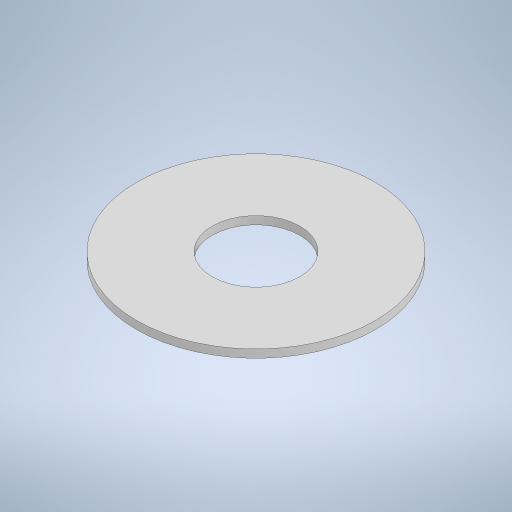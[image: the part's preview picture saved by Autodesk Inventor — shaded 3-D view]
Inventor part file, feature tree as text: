
AUTODESK INVENTOR PART (.ipt)
format: ipt  version: 2024.2 (Build 282272000, 272)  size: 224,256 bytes
history: native  units: mm
features: extrude x1, sketch x1
ambient origin geometry x8: Origin, YZ Plane, XZ Plane, XY Plane, X Axis, Y Axis, Z Axis, Center Point
bodies: Solid1 (feature_tree)
feature tree (2):
  extrude  "Extrusion1"  Depth=0.2mm
  sketch  "Sketch1"  dims[d0=2.2mm d1=6.0mm d2=0.2mm d3=0.0mm]
